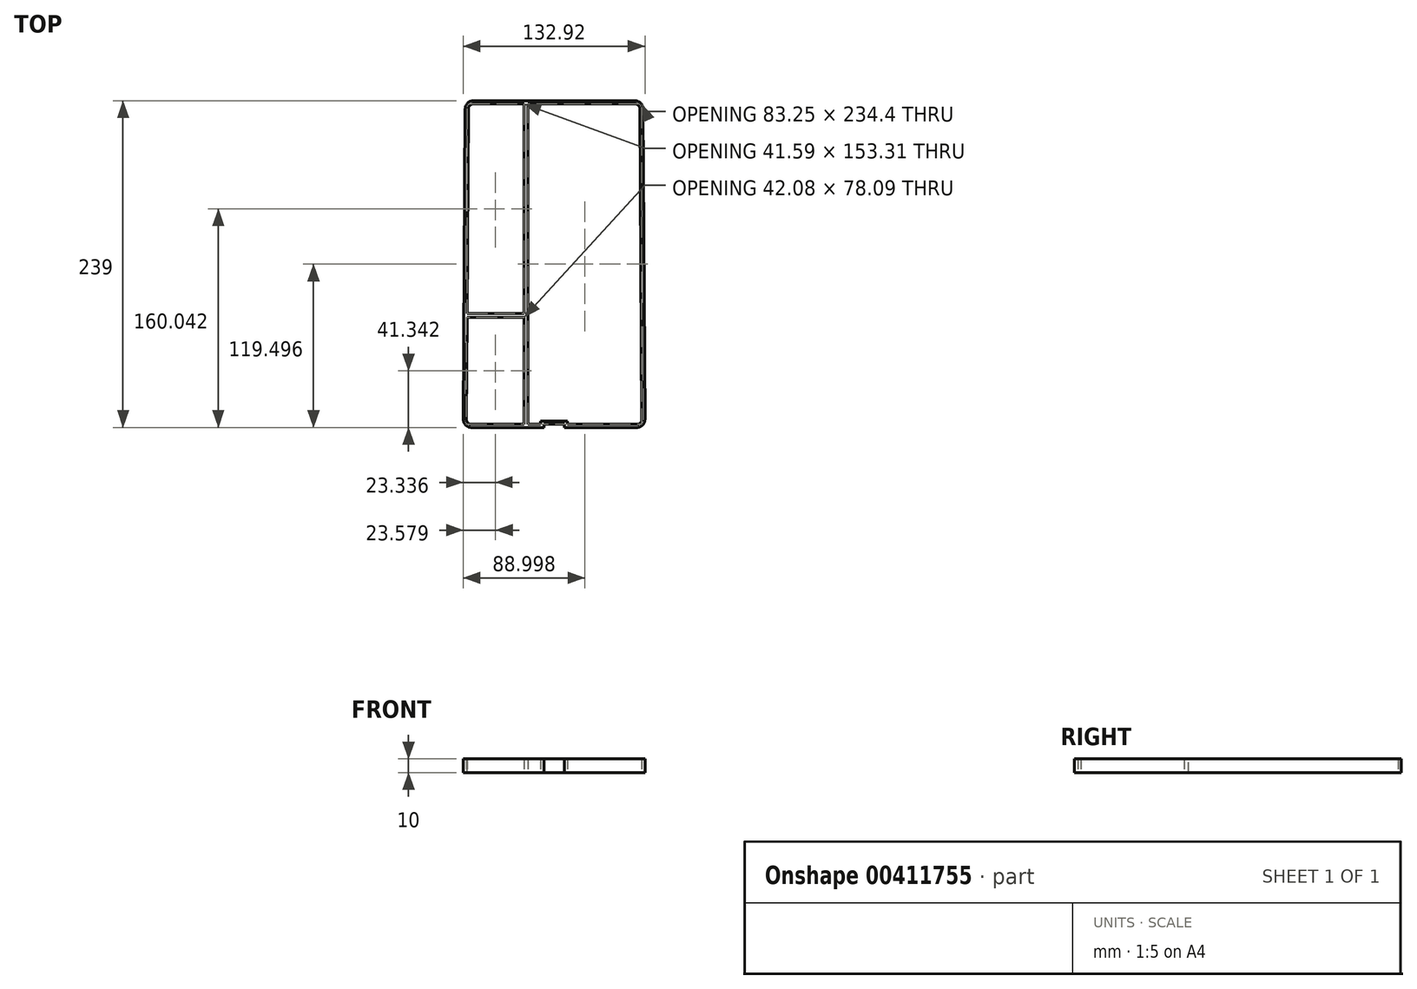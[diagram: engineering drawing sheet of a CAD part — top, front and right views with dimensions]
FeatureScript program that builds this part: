
annotation { "Feature Type Name" : "Feature", "Feature Type Description" : "" }
export const myFeature = defineFeature(function(context is Context, id is Id, definition is map)
    precondition{}
    {
        {
            var Q0;
            Q0=qCreatedBy(makeId("Top.planeOp"),FACE);
            var sketch = newSketch(context, id + "F0", { "sketchPlane" : qUnion([Q0])});
            skLineSegment(sketch, "E0", {"start": v(-61.33, -99.15) * mm, "end": v(-8.37, -99.15) * mm});
            skLineSegment(sketch, "E1", {"start": v(-59.9, 139.85) * mm, "end": v(58.17, 139.85) * mm});
            skLineSegment(sketch, "E2", {"start": v(-65.9, 133.88) * mm, "end": v(-67.33, -93.12) * mm});
            skLineSegment(sketch, "E3", {"start": v(64.17, 133.88) * mm, "end": v(65.6, -93.12) * mm});
            skPoint(sketch, "E4", {"position": v(-0.87, 139.85) * mm});
            skPoint(sketch, "E5", {"position": v(-0.87, -99.15) * mm});
            skPoint(sketch, "E6.visualSharp", {"position": v(-65.87, 139.85) * mm});
            skArc(sketch, "E6.filletArc", {"start": v(-59.9, 139.85) * mm, "mid": v(-64.14, 138.1) * mm, "end": v(-65.9, 133.88) * mm});
            skPoint(sketch, "E7.visualSharp", {"position": v(-67.37, -99.15) * mm});
            skArc(sketch, "E7.filletArc", {"start": v(-67.33, -93.12) * mm, "mid": v(-65.59, -97.38) * mm, "end": v(-61.33, -99.15) * mm});
            skPoint(sketch, "E8.visualSharp", {"position": v(65.63, -99.15) * mm});
            skArc(sketch, "E8.filletArc", {"start": v(59.6, -99.15) * mm, "mid": v(63.85, -97.38) * mm, "end": v(65.6, -93.12) * mm});
            skPoint(sketch, "E9.visualSharp", {"position": v(64.13, 139.85) * mm});
            skArc(sketch, "E9.filletArc", {"start": v(64.17, 133.88) * mm, "mid": v(62.4, 138.1) * mm, "end": v(58.17, 139.85) * mm});
            skLineSegment(sketch, "E10.0", {"start": v(-61.33, -96.85) * mm, "end": v(-10.67, -96.85) * mm});
            skArc(sketch, "E10.1", {"start": v(-65.03, -93.13) * mm, "mid": v(-63.96, -95.76) * mm, "end": v(-61.33, -96.85) * mm});
            skArc(sketch, "E10.2", {"start": v(59.6, -96.85) * mm, "mid": v(62.22, -95.76) * mm, "end": v(63.3, -93.13) * mm});
            skLineSegment(sketch, "E10.3", {"start": v(-63.6, 133.87) * mm, "end": v(-65.03, -93.13) * mm});
            skLineSegment(sketch, "E10.4", {"start": v(61.87, 133.87) * mm, "end": v(63.3, -93.13) * mm});
            skArc(sketch, "E10.5", {"start": v(61.87, 133.87) * mm, "mid": v(60.78, 136.47) * mm, "end": v(58.17, 137.55) * mm});
            skLineSegment(sketch, "E10.6", {"start": v(-59.9, 137.55) * mm, "end": v(58.17, 137.55) * mm});
            skArc(sketch, "E10.7", {"start": v(-59.9, 137.55) * mm, "mid": v(-62.52, 136.47) * mm, "end": v(-63.6, 133.87) * mm});
            skLineSegment(sketch, "E11", {"start": v(-8.37, -96.85) * mm, "end": v(-8.37, -99.15) * mm});
            skLineSegment(sketch, "E12", {"start": v(6.63, -96.85) * mm, "end": v(6.63, -99.15) * mm});
            skLineSegment(sketch, "E13.bottom", {"start": v(-8.37, -96.85) * mm, "end": v(6.63, -96.85) * mm});
            skLineSegment(sketch, "E13.top", {"start": v(-10.67, -94.55) * mm, "end": v(8.93, -94.55) * mm});
            skLineSegment(sketch, "E13.left", {"start": v(-10.67, -96.85) * mm, "end": v(-10.67, -94.55) * mm});
            skLineSegment(sketch, "E13.right", {"start": v(8.93, -96.85) * mm, "end": v(8.93, -94.55) * mm});
            skLineSegment(sketch, "E14.trimOffspring", {"start": v(8.93, -96.85) * mm, "end": v(59.6, -96.85) * mm});
            skLineSegment(sketch, "E15.trimOffspring", {"start": v(6.63, -99.15) * mm, "end": v(59.6, -99.15) * mm});
            skSolve(sketch);
        }
        {
            var Q0;
            Q0 = qSketchRegion(id + "F0", true);
            extrude(context, id + "F1", {"entities" : qUnion([Q0]), "depth" : 10 * mm});
        }
        {
            var Q0;
            Q0=makeQuery(id+"F0.imprint","IMPRINT",FACE,{"disambiguationData":[TD([[makeQuery(id+"F0.imprint","IMPRINT",EDGE,{"derivedFrom":sQuery(id+"F0.wireOp",EDGE,"E0")}),1.0]])]});
            var sketch = newSketch(context, id + "F2", { "sketchPlane" : qUnion([Q0])});
            skLineSegment(sketch, "E16.bottom", {"start": v(-63.96, -18.76) * mm, "end": v(-22.96, -18.76) * mm});
            skLineSegment(sketch, "E16.top", {"start": v(-63.96, -95.76) * mm, "end": v(-22.96, -95.76) * mm, "construction": true});
            skLineSegment(sketch, "E16.left", {"start": v(-63.96, -18.76) * mm, "end": v(-63.96, -95.76) * mm, "construction": true});
            skLineSegment(sketch, "E16.right", {"start": v(-22.96, -18.76) * mm, "end": v(-22.96, -95.76) * mm});
            skLineSegment(sketch, "E17.bottom", {"start": v(-64.57, -15.76) * mm, "end": v(-22.96, -15.76) * mm});
            skLineSegment(sketch, "E17.top", {"start": v(-64.57, -18.76) * mm, "end": v(-22.96, -18.76) * mm});
            skLineSegment(sketch, "E17.left", {"start": v(-64.57, -15.76) * mm, "end": v(-64.57, -18.76) * mm});
            skLineSegment(sketch, "E18.bottom", {"start": v(-22.96, -96.85) * mm, "end": v(-19.96, -96.85) * mm});
            skLineSegment(sketch, "E18.top", {"start": v(-22.96, 137.55) * mm, "end": v(-19.96, 137.55) * mm});
            skLineSegment(sketch, "E18.left", {"start": v(-22.96, -96.85) * mm, "end": v(-22.96, -18.76) * mm});
            skLineSegment(sketch, "E18.right", {"start": v(-19.96, -96.85) * mm, "end": v(-19.96, -18.76) * mm});
            skLineSegment(sketch, "E19.trimOffspring", {"start": v(-22.96, -15.76) * mm, "end": v(-22.96, 137.55) * mm});
            skLineSegment(sketch, "E20.trimOffspring", {"start": v(-19.96, -18.76) * mm, "end": v(-19.96, 137.55) * mm});
            skSolve(sketch);
        }
        {
            var Q0;
            Q0 = qSketchRegion(id + "F2", true);
            extrude(context, id + "F3", {"entities" : qUnion([Q0]), "operationType" : NewBodyOperationType.ADD, "depth" : 10 * mm});
        }
    });
